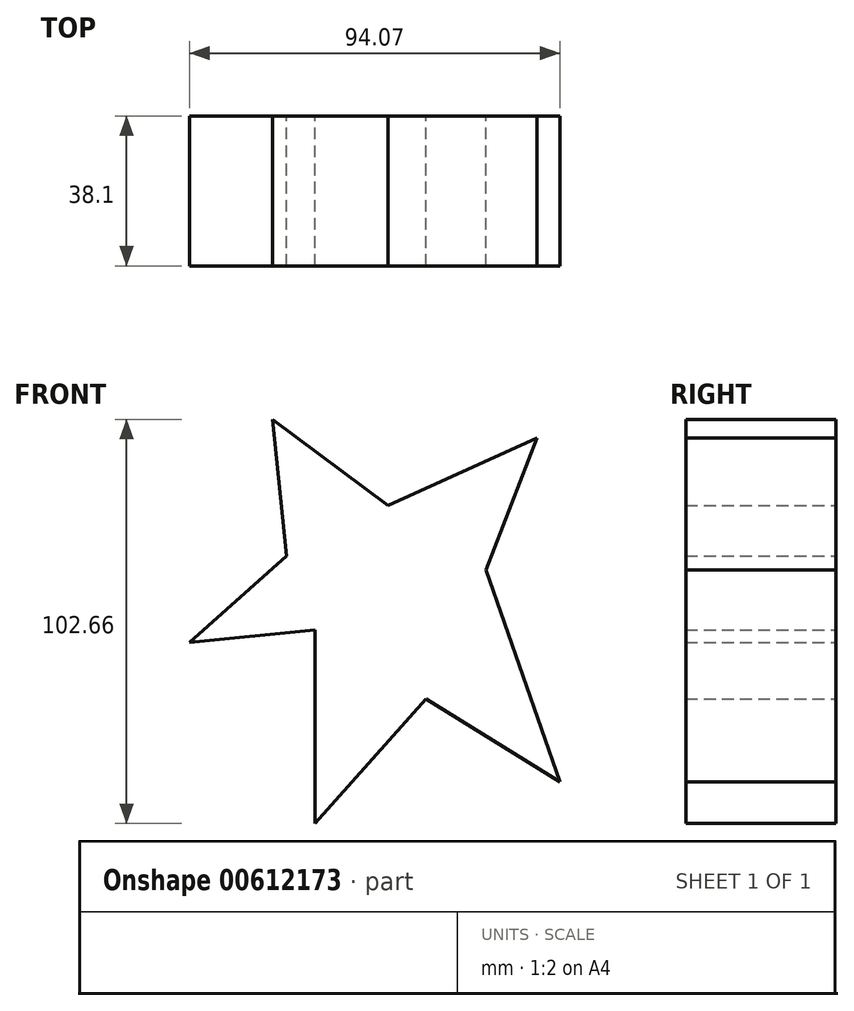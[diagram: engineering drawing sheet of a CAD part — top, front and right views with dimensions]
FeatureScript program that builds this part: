
annotation { "Feature Type Name" : "Feature", "Feature Type Description" : "" }
export const myFeature = defineFeature(function(context is Context, id is Id, definition is map)
    precondition{}
    {
        {
            var Q0;
            Q0=qCreatedBy(makeId("Front.planeOp"),FACE);
            var sketch = newSketch(context, id + "F0", { "sketchPlane" : qUnion([Q0])});
            skLineSegment(sketch, "E0", {"start": v(0, 0) * mm, "end": v(28.3, 31.62) * mm});
            skLineSegment(sketch, "E1", {"start": v(28.3, 31.62) * mm, "end": v(62.26, 10.54) * mm});
            skLineSegment(sketch, "E2", {"start": v(62.26, 10.54) * mm, "end": v(43.52, 64.4) * mm});
            skLineSegment(sketch, "E3", {"start": v(43.52, 64.4) * mm, "end": v(56.4, 97.98) * mm});
            skLineSegment(sketch, "E4", {"start": v(56.4, 97.98) * mm, "end": v(18.54, 80.8) * mm});
            skLineSegment(sketch, "E5", {"start": v(18.54, 80.8) * mm, "end": v(-10.73, 102.66) * mm});
            skLineSegment(sketch, "E6", {"start": v(-10.73, 102.66) * mm, "end": v(-7.22, 67.92) * mm});
            skLineSegment(sketch, "E7", {"start": v(-7.22, 67.92) * mm, "end": v(-31.81, 46.06) * mm});
            skLineSegment(sketch, "E8", {"start": v(-31.81, 46.06) * mm, "end": v(0, 49.19) * mm});
            skLineSegment(sketch, "E9", {"start": v(0, 49.19) * mm, "end": v(0, 0) * mm});
            skSolve(sketch);
        }
        {
            var Q0;
            Q0=makeQuery(id+"F0.imprint","IMPRINT",FACE,{"disambiguationData":[TD([[makeQuery(id+"F0.imprint","IMPRINT",EDGE,{"derivedFrom":sQuery(id+"F0.wireOp",EDGE,"E0")}),1.0]])]});
            extrude(context, id + "F1", {"entities" : qUnion([Q0]), "depth" : 25.4 * mm, "offsetDistance" : 25.4 * mm, "symmetric" : true});
        }
        {
            var Q0;
            Q0 = qSketchRegion(id + "F0", true);
            extrude(context, id + "F2", {"entities" : qUnion([Q0]), "operationType" : NewBodyOperationType.ADD, "depth" : 25.4 * mm, "offsetDistance" : 25.4 * mm});
        }
    });
